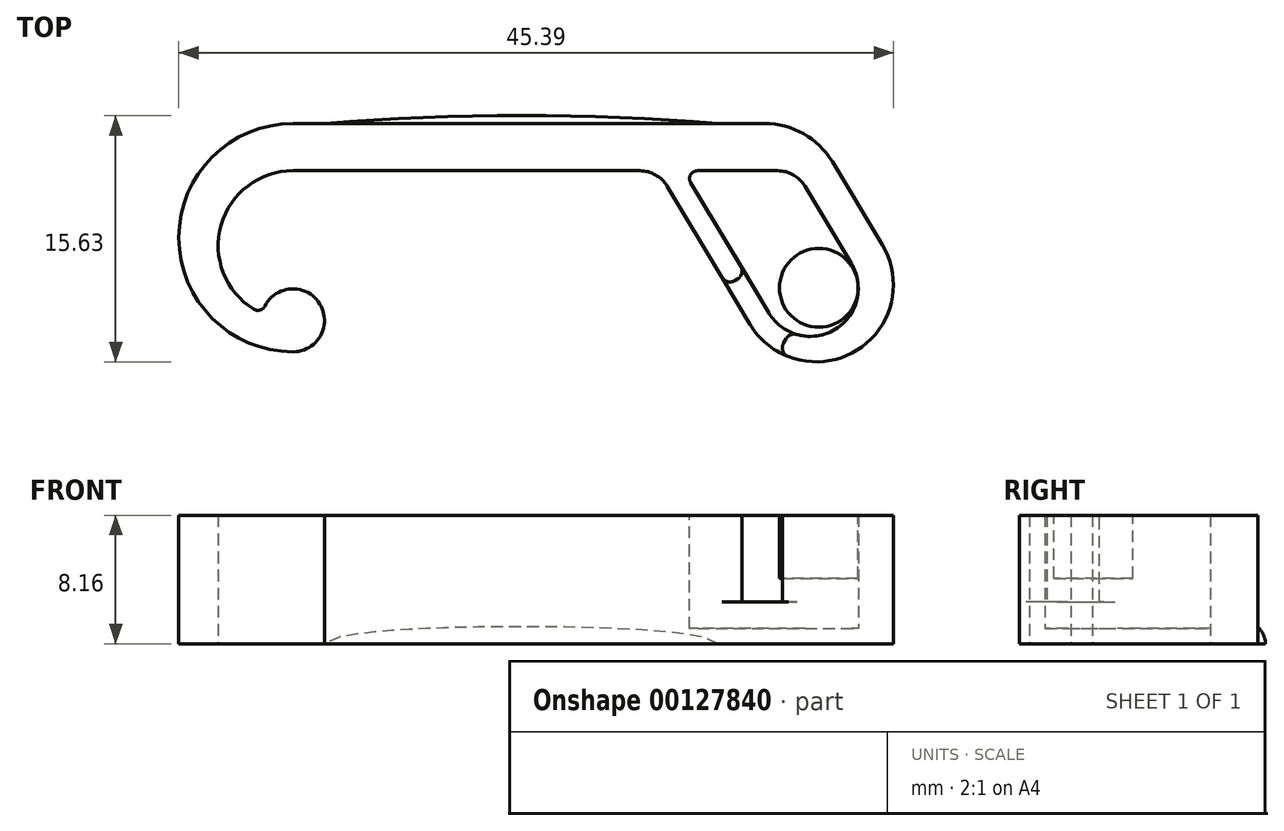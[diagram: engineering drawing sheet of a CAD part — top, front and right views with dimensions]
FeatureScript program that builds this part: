
annotation { "Feature Type Name" : "Feature", "Feature Type Description" : "" }
export const myFeature = defineFeature(function(context is Context, id is Id, definition is map)
    precondition{}
    {
        {
            var Q0;
            Q0=qCreatedBy(makeId("Top.planeOp"),FACE);
            var sketch = newSketch(context, id + "F0", { "sketchPlane" : qUnion([Q0])});
            skLineSegment(sketch, "E0", {"start": v(-39.98, 9.47) * mm, "end": v(-7.18, 9.47) * mm});
            skLineSegment(sketch, "E1", {"start": v(-7.18, 9.47) * mm, "end": v(-2.54, 1.75) * mm});
            skArc(sketch, "E2", {"start": v(-39.98, 9.47) * mm, "mid": v(-47.23, 2.22) * mm, "end": v(-39.98, -5.03) * mm});
            skArc(sketch, "E3", {"start": v(-2.54, 1.75) * mm, "mid": v(-4.22, -4.97) * mm, "end": v(-10.94, -3.3) * mm});
            skLineSegment(sketch, "E4", {"start": v(-2.54, 1.75) * mm, "end": v(-11.71, -3.76) * mm, "construction": true});
            skLineSegment(sketch, "E5", {"start": v(-10.94, -3.3) * mm, "end": v(-16.8, 6.47) * mm});
            skLineSegment(sketch, "E6", {"start": v(-39.98, 9.47) * mm, "end": v(-39.98, -5.03) * mm, "construction": true});
            skLineSegment(sketch, "E7", {"start": v(-39.98, 6.47) * mm, "end": v(-16.8, 6.47) * mm});
            skLineSegment(sketch, "E8.0", {"start": v(-8.06, 6.47) * mm, "end": v(-4.51, 0.57) * mm});
            skLineSegment(sketch, "E9.0", {"start": v(-9.74, -2.58) * mm, "end": v(-15.17, 6.47) * mm});
            skLineSegment(sketch, "E10.trimOffspring", {"start": v(-15.17, 6.47) * mm, "end": v(-8.06, 6.47) * mm});
            skArc(sketch, "E11", {"start": v(-39.98, -5.03) * mm, "mid": v(-38.42, -1.78) * mm, "end": v(-41.93, -2.61) * mm});
            skArc(sketch, "E12", {"start": v(-39.98, 6.47) * mm, "mid": v(-44.62, 2.72) * mm, "end": v(-41.93, -2.61) * mm});
            skArc(sketch, "E13", {"start": v(-9.74, -2.58) * mm, "mid": v(-5.55, -3.62) * mm, "end": v(-4.51, 0.57) * mm});
            skLineSegment(sketch, "E14", {"start": v(-37.98, -2.84) * mm, "end": v(-37.98, -7.84) * mm, "construction": true});
            skLineSegment(sketch, "E15", {"start": v(-4.08, 2.14) * mm, "end": v(-4.08, -9.58) * mm, "construction": true});
            skSolve(sketch);
        }
        {
            var Q0;
            Q0=qSketchRegion(id+"F0",true);
            extrude(context, id + "F1", {"entities" : qUnion([Q0]), "endBound" : BoundingType.SYMMETRIC, "depth" : 16.4 * mm});
        }
        {
            var Q0;
            Q0=makeQuery(id+"F0.imprint","IMPRINT",FACE,{"disambiguationData":[TD([[makeQuery(id+"F0.imprint","IMPRINT",EDGE,{"derivedFrom":sQuery(id+"F0.wireOp",EDGE,"E8.0")}),-1.0]])]});
            extrude(context, id + "F2", {"entities" : qUnion([Q0]), "operationType" : NewBodyOperationType.ADD, "endBound" : BoundingType.SYMMETRIC, "depth" : 2 * mm});
        }
        {
            var Q0;
            Q0=makeQuery(id+"F1.opExtrude","CAP_FACE",FACE,{"disambiguationData":[OSD([sQuery(id+"F0.wireOp",EDGE,"E0"),sQuery(id+"F0.wireOp",EDGE,"E1"),sQuery(id+"F0.wireOp",EDGE,"E2"),sQuery(id+"F0.wireOp",EDGE,"E3"),sQuery(id+"F0.wireOp",EDGE,"E5"),sQuery(id+"F0.wireOp",EDGE,"E7"),sQuery(id+"F0.wireOp",EDGE,"E8.0"),sQuery(id+"F0.wireOp",EDGE,"E9.0"),sQuery(id+"F0.wireOp",EDGE,"E10.trimOffspring"),sQuery(id+"F0.wireOp",EDGE,"E11"),sQuery(id+"F0.wireOp",EDGE,"E12"),sQuery(id+"F0.wireOp",EDGE,"E13")])],"isStart":false});
            var sketch = newSketch(context, id + "F3", { "sketchPlane" : qUnion([Q0])});
            skPoint(sketch, "E16", {"position": v(-6.74, -0.77) * mm});
            skLineSegment(sketch, "E17", {"start": v(-6.74, -0.77) * mm, "end": v(-10.04, -6.68) * mm});
            skLineSegment(sketch, "E18", {"start": v(-8.23, 1.7) * mm, "end": v(-13.26, -1.32) * mm});
            skLineSegment(sketch, "E19", {"start": v(-8.23, 1.7) * mm, "end": v(-6.74, -0.77) * mm});
            skLineSegment(sketch, "E20", {"start": v(-13.26, -1.32) * mm, "end": v(-10.04, -6.68) * mm});
            skArc(sketch, "E21.0", {"start": v(-2.5, 1.68) * mm, "mid": v(-4.29, -5.02) * mm, "end": v(-10.98, -3.22) * mm, "construction": true});
            skLineSegment(sketch, "E22", {"start": v(-6.74, -0.77) * mm, "end": v(-13.86, 11.08) * mm, "construction": true});
            skLineSegment(sketch, "E23.0", {"start": v(-40.2, 9.47) * mm, "end": v(-8.2, 9.47) * mm, "construction": true});
            skPoint(sketch, "E24", {"position": v(-13.36, 9.47) * mm});
            skSolve(sketch);
        }
        {
            var Q0;
            Q0=qSketchRegion(id+"F3",true);
            extrude(context, id + "F4", {"entities" : qUnion([Q0]), "operationType" : NewBodyOperationType.REMOVE, "oppositeDirection" : true, "depth" : 5.5 * mm});
        }
        {
            var Q0;
            Q0=makeQuery(id+"F1.opExtrude","CAP_FACE",FACE,{"disambiguationData":[OSD([sQuery(id+"F0.wireOp",EDGE,"E0"),sQuery(id+"F0.wireOp",EDGE,"E1"),sQuery(id+"F0.wireOp",EDGE,"E2"),sQuery(id+"F0.wireOp",EDGE,"E3"),sQuery(id+"F0.wireOp",EDGE,"E5"),sQuery(id+"F0.wireOp",EDGE,"E7"),sQuery(id+"F0.wireOp",EDGE,"E8.0"),sQuery(id+"F0.wireOp",EDGE,"E9.0"),sQuery(id+"F0.wireOp",EDGE,"E10.trimOffspring"),sQuery(id+"F0.wireOp",EDGE,"E11"),sQuery(id+"F0.wireOp",EDGE,"E12"),sQuery(id+"F0.wireOp",EDGE,"E13")])],"isStart":true});
            var sketch = newSketch(context, id + "F15", { "sketchPlane" : qUnion([Q0])});
            skLineSegment(sketch, "E25.0", {"start": v(-8.7, -1.42) * mm, "end": v(-13.39, 1.4) * mm});
            skLineSegment(sketch, "E26.0", {"start": v(-13.32, 1.21) * mm, "end": v(-10.9, 5.24) * mm});
            skLineSegment(sketch, "E27.0", {"start": v(-7.02, 1.28) * mm, "end": v(-9.79, 6.22) * mm});
            skLineSegment(sketch, "E28.0", {"start": v(-8.24, -1.73) * mm, "end": v(-6.58, 1.04) * mm});
            skSolve(sketch);
        }
        {
            var Q0;
            {var subQ0=makeQuery(id+"F1.opExtrude","CAP_EDGE",EDGE,{"disambiguationData":[OSD([sQuery(id+"F0.wireOp",EDGE,"E5")])],"isStart":true});var subQ5=sQuery(id+"F15.wireOp",EDGE,"E25.0");var subQ6=makeQuery(id+"F15.imprint","INTERSECT",VERTEX,{"derivedFrom":[subQ0,subQ5]});Q0=makeQuery(id+"F15.imprint","IMPRINT",FACE,{"disambiguationData":[TD([[makeQuery(id+"F15.imprint","IMPRINT",EDGE,{"disambiguationData":[TD([[subQ6,1.0]])],"derivedFrom":subQ5}),-1.0]])]});}
            extrude(context, id + "F16", {"entities" : qUnion([Q0]), "operationType" : NewBodyOperationType.REMOVE, "oppositeDirection" : true, "depth" : 5.5 * mm});
        }
        {
            var Q0;
            Q0=makeQuery(id+"F1.opExtrude","SWEPT_EDGE",EDGE,{"disambiguationData":[OSD([sQuery(id+"F0.wireOp",EDGE,"E5"),sQuery(id+"F0.wireOp",EDGE,"E7")])]});
            fillet(context, id + "F5", {"entities" : qUnion([Q0]), "radius" : 2 * mm, "tangentPropagation" : true, "allowEdgeOverflow" : false});
        }
        {
            var Q0;
            {var subQ0=sQuery(id+"F0.wireOp",EDGE,"E13");var subQ1=sQuery(id+"F0.wireOp",EDGE,"E10.trimOffspring");var subQ2=sQuery(id+"F0.wireOp",EDGE,"E9.0");var subQ3=sQuery(id+"F0.wireOp",EDGE,"E8.0");Q0=makeQuery(id+"F2.boolean.opBoolean","SPLIT",EDGE,{"disambiguationData":[TD([makeQuery(id+"F2.opExtrude","CAP_FACE",FACE,{"disambiguationData":[OSD([subQ3,subQ2,subQ1,subQ0])],"isStart":true})])],"derivedFrom":makeQuery(id+"F1.opExtrude","SWEPT_EDGE",EDGE,{"disambiguationData":[OSD([subQ2,subQ1])]})});}
            var Q1;
            {var subQ0=sQuery(id+"F0.wireOp",EDGE,"E13");var subQ1=sQuery(id+"F0.wireOp",EDGE,"E10.trimOffspring");var subQ2=sQuery(id+"F0.wireOp",EDGE,"E9.0");var subQ3=sQuery(id+"F0.wireOp",EDGE,"E8.0");Q1=makeQuery(id+"F2.boolean.opBoolean","SPLIT",EDGE,{"disambiguationData":[TD([makeQuery(id+"F2.opExtrude","CAP_FACE",FACE,{"disambiguationData":[OSD([subQ3,subQ2,subQ1,subQ0])],"isStart":false})])],"derivedFrom":makeQuery(id+"F1.opExtrude","SWEPT_EDGE",EDGE,{"disambiguationData":[OSD([subQ2,subQ1])]})});}
            fillet(context, id + "F17", {"entities" : qUnion([Q0, Q1]), "radius" : 0.5 * mm, "tangentPropagation" : true, "allowEdgeOverflow" : false});
        }
        {
            var Q0;
            {var subQ0=sQuery(id+"F0.wireOp",EDGE,"E13");var subQ1=sQuery(id+"F0.wireOp",EDGE,"E10.trimOffspring");var subQ2=sQuery(id+"F0.wireOp",EDGE,"E9.0");var subQ3=sQuery(id+"F0.wireOp",EDGE,"E8.0");Q0=makeQuery(id+"F2.boolean.opBoolean","SPLIT",EDGE,{"disambiguationData":[TD([makeQuery(id+"F2.opExtrude","CAP_FACE",FACE,{"disambiguationData":[OSD([subQ3,subQ2,subQ1,subQ0])],"isStart":true})])],"derivedFrom":makeQuery(id+"F1.opExtrude","SWEPT_EDGE",EDGE,{"disambiguationData":[OSD([subQ3,subQ1])]})});}
            var Q1;
            {var subQ0=sQuery(id+"F0.wireOp",EDGE,"E13");var subQ1=sQuery(id+"F0.wireOp",EDGE,"E10.trimOffspring");var subQ2=sQuery(id+"F0.wireOp",EDGE,"E9.0");var subQ3=sQuery(id+"F0.wireOp",EDGE,"E8.0");Q1=makeQuery(id+"F2.boolean.opBoolean","SPLIT",EDGE,{"disambiguationData":[TD([makeQuery(id+"F2.opExtrude","CAP_FACE",FACE,{"disambiguationData":[OSD([subQ3,subQ2,subQ1,subQ0])],"isStart":false})])],"derivedFrom":makeQuery(id+"F1.opExtrude","SWEPT_EDGE",EDGE,{"disambiguationData":[OSD([subQ3,subQ1])]})});}
            fillet(context, id + "F18", {"entities" : qUnion([Q0, Q1]), "radius" : 2 * mm, "tangentPropagation" : true, "allowEdgeOverflow" : false});
        }
        {
            var Q0;
            Q0=makeQuery(id+"F1.opExtrude","SWEPT_EDGE",EDGE,{"disambiguationData":[OSD([sQuery(id+"F0.wireOp",EDGE,"E0"),sQuery(id+"F0.wireOp",EDGE,"E1")])]});
            fillet(context, id + "F19", {"entities" : qUnion([Q0]), "radius" : 5 * mm, "tangentPropagation" : true, "allowEdgeOverflow" : false});
        }
        {
            var Q0;
            Q0=makeQuery(id+"F1.opExtrude","SWEPT_EDGE",EDGE,{"disambiguationData":[OSD([sQuery(id+"F0.wireOp",EDGE,"E11"),sQuery(id+"F0.wireOp",EDGE,"E12")])]});
            fillet(context, id + "F20", {"entities" : qUnion([Q0]), "radius" : 0.5 * mm, "tangentPropagation" : true, "allowEdgeOverflow" : false});
        }
        {
            var Q0;
            Q0=makeQuery(id+"F4.boolean.opBoolean","INTERSECT",EDGE,{"derivedFrom":[makeQuery(id+"F1.opExtrude","SWEPT_FACE",FACE,{"disambiguationData":[OSD([sQuery(id+"F0.wireOp",EDGE,"E5")])]}),makeQuery(id+"F4.opExtrude","SWEPT_FACE",FACE,{"disambiguationData":[OSD([sQuery(id+"F3.wireOp",EDGE,"E18")])]})]});
            var Q1;
            {var subQ0=sQuery(id+"F0.wireOp",EDGE,"E13");var subQ1=sQuery(id+"F0.wireOp",EDGE,"E10.trimOffspring");var subQ2=sQuery(id+"F0.wireOp",EDGE,"E9.0");var subQ3=sQuery(id+"F0.wireOp",EDGE,"E8.0");Q1=makeQuery(id+"F4.boolean.opBoolean","INTERSECT",EDGE,{"derivedFrom":[makeQuery(id+"F2.boolean.opBoolean","SPLIT",FACE,{"disambiguationData":[TD([makeQuery(id+"F2.opExtrude","CAP_FACE",FACE,{"disambiguationData":[OSD([subQ3,subQ2,subQ1,subQ0])],"isStart":false})])],"derivedFrom":makeQuery(id+"F1.opExtrude","SWEPT_FACE",FACE,{"disambiguationData":[OSD([subQ2])]})}),makeQuery(id+"F4.opExtrude","SWEPT_FACE",FACE,{"disambiguationData":[OSD([sQuery(id+"F3.wireOp",EDGE,"E18")])]})]});}
            var Q2;
            {var subQ0=sQuery(id+"F0.wireOp",EDGE,"E13");var subQ1=sQuery(id+"F0.wireOp",EDGE,"E10.trimOffspring");var subQ2=sQuery(id+"F0.wireOp",EDGE,"E9.0");var subQ3=sQuery(id+"F0.wireOp",EDGE,"E8.0");Q2=makeQuery(id+"F4.boolean.opBoolean","INTERSECT",EDGE,{"derivedFrom":[makeQuery(id+"F2.boolean.opBoolean","SPLIT",FACE,{"disambiguationData":[TD([makeQuery(id+"F2.opExtrude","CAP_FACE",FACE,{"disambiguationData":[OSD([subQ3,subQ2,subQ1,subQ0])],"isStart":false})])],"derivedFrom":makeQuery(id+"F1.opExtrude","SWEPT_FACE",FACE,{"disambiguationData":[OSD([subQ0])]})}),makeQuery(id+"F4.opExtrude","SWEPT_FACE",FACE,{"disambiguationData":[OSD([sQuery(id+"F3.wireOp",EDGE,"E17")])]})]});}
            var Q3;
            Q3=makeQuery(id+"F4.boolean.opBoolean","INTERSECT",EDGE,{"derivedFrom":[makeQuery(id+"F1.opExtrude","SWEPT_FACE",FACE,{"disambiguationData":[OSD([sQuery(id+"F0.wireOp",EDGE,"E3")])]}),makeQuery(id+"F4.opExtrude","SWEPT_FACE",FACE,{"disambiguationData":[OSD([sQuery(id+"F3.wireOp",EDGE,"E17")])]})]});
            var Q4;
            Q4=makeQuery(id+"F16.boolean.opBoolean","COPY",EDGE,{"derivedFrom":makeQuery(id+"F16.opExtrude","SWEPT_EDGE",EDGE,{"disambiguationData":[OSD([sQuery(id+"F0.wireOp",EDGE,"E3"),sQuery(id+"F15.wireOp",EDGE,"E27.0")])]})});
            var Q5;
            Q5=makeQuery(id+"F16.boolean.opBoolean","COPY",EDGE,{"derivedFrom":makeQuery(id+"F16.opExtrude","SWEPT_EDGE",EDGE,{"disambiguationData":[OSD([sQuery(id+"F0.wireOp",EDGE,"E13"),sQuery(id+"F15.wireOp",EDGE,"E27.0")])]})});
            var Q6;
            Q6=makeQuery(id+"F16.boolean.opBoolean","COPY",EDGE,{"derivedFrom":makeQuery(id+"F16.opExtrude","SWEPT_EDGE",EDGE,{"disambiguationData":[OSD([sQuery(id+"F0.wireOp",EDGE,"E5"),sQuery(id+"F15.wireOp",EDGE,"E25.0")])]})});
            var Q7;
            Q7=makeQuery(id+"F16.boolean.opBoolean","COPY",EDGE,{"derivedFrom":makeQuery(id+"F16.opExtrude","SWEPT_EDGE",EDGE,{"disambiguationData":[OSD([sQuery(id+"F0.wireOp",EDGE,"E9.0"),sQuery(id+"F15.wireOp",EDGE,"E25.0")])]})});
            fillet(context, id + "F6", {"entities" : qUnion([Q0, Q1, Q2, Q3, Q4, Q5, Q6, Q7]), "radius" : 0.6 * mm, "tangentPropagation" : true, "allowEdgeOverflow" : false});
        }
        {
            var Q0;
            Q0=qCreatedBy(makeId("Top.planeOp"),FACE);
            var sketch = newSketch(context, id + "F7", { "sketchPlane" : qUnion([Q0])});
            skLineSegment(sketch, "E29", {"start": v(-37.96, -2.7) * mm, "end": v(-37.96, 14.25) * mm, "construction": true});
            skLineSegment(sketch, "E30", {"start": v(-12.96, 3.52) * mm, "end": v(-12.96, 12.6) * mm, "construction": true});
            skLineSegment(sketch, "E31.0", {"start": v(-39.98, 9.47) * mm, "end": v(-10, 9.47) * mm});
            skPoint(sketch, "E32", {"position": v(-37.96, 9.47) * mm});
            skPoint(sketch, "E33", {"position": v(-12.96, 9.47) * mm});
            skArc(sketch, "E34", {"start": v(-12.96, 9.47) * mm, "mid": v(-25.46, 9.97) * mm, "end": v(-37.96, 9.47) * mm});
            skSolve(sketch);
        }
        {
            var Q0;
            Q0 = qSketchRegion(id + "F7", true);
            extrude(context, id + "F8", {"entities" : qUnion([Q0]), "operationType" : NewBodyOperationType.ADD, "endBound" : BoundingType.SYMMETRIC, "depth" : 3 * mm});
        }
        {
            var Q0;
            Q0=makeQuery(id+"F8.opExtrude","CAP_EDGE",EDGE,{"disambiguationData":[OSD([sQuery(id+"F7.wireOp",EDGE,"E34")])],"isStart":false});
            fillet(context, id + "F9", {"entities" : qUnion([Q0]), "radius" : 1.5 * mm, "tangentPropagation" : true, "allowEdgeOverflow" : false});
        }
        {
            var Q0;
            Q0=makeQuery(id+"F8.opExtrude","CAP_EDGE",EDGE,{"disambiguationData":[OSD([sQuery(id+"F7.wireOp",EDGE,"E34")])],"isStart":true});
            fillet(context, id + "F10", {"entities" : qUnion([Q0]), "radius" : 1.5 * mm, "tangentPropagation" : true, "allowEdgeOverflow" : false});
        }
        {
            var Q0;
            Q0=makeQuery(id+"F1.opExtrude","CAP_FACE",FACE,{"disambiguationData":[OSD([sQuery(id+"F0.wireOp",EDGE,"E0"),sQuery(id+"F0.wireOp",EDGE,"E1"),sQuery(id+"F0.wireOp",EDGE,"E2"),sQuery(id+"F0.wireOp",EDGE,"E3"),sQuery(id+"F0.wireOp",EDGE,"E5"),sQuery(id+"F0.wireOp",EDGE,"E7"),sQuery(id+"F0.wireOp",EDGE,"E8.0"),sQuery(id+"F0.wireOp",EDGE,"E9.0"),sQuery(id+"F0.wireOp",EDGE,"E10.trimOffspring"),sQuery(id+"F0.wireOp",EDGE,"E11"),sQuery(id+"F0.wireOp",EDGE,"E12"),sQuery(id+"F0.wireOp",EDGE,"E13")])],"isStart":false});
            var sketch = newSketch(context, id + "F11", { "sketchPlane" : qUnion([Q0])});
            skCircle(sketch, "E35", {"center": v(-6.58, -0.97) * mm, "radius": 2.5 * mm});
            skArc(sketch, "E36.0", {"start": v(-39.98, -5.03) * mm, "mid": v(-38.27, -1.99) * mm, "end": v(-41.76, -2.13) * mm, "construction": true});
            skArc(sketch, "E37.0", {"start": v(-7.97, -3.93) * mm, "mid": v(-4.7, -2.86) * mm, "end": v(-4.51, 0.57) * mm, "construction": true});
            skLineSegment(sketch, "E38.0", {"start": v(-39.98, 9.47) * mm, "end": v(-10, 9.47) * mm, "construction": true});
            skLineSegment(sketch, "E39", {"start": v(-39.98, -3.03) * mm, "end": v(-1.08, -0.63) * mm, "construction": true});
            skSolve(sketch);
        }
        {
            var Q0;
            Q0 = qSketchRegion(id + "F11", true);
            extrude(context, id + "F12", {"entities" : qUnion([Q0]), "oppositeDirection" : true, "depth" : 4 * mm});
        }
        {
            var Q0;
            Q0=qCreatedBy(makeId("Front.planeOp"),FACE);
            var sketch = newSketch(context, id + "F13", { "sketchPlane" : qUnion([Q0])});
            skLineSegment(sketch, "E40.bottom", {"start": v(-48.32, 0.04) * mm, "end": v(-1.2, 0.04) * mm});
            skLineSegment(sketch, "E40.top", {"start": v(-48.32, -11.32) * mm, "end": v(-1.2, -11.32) * mm});
            skLineSegment(sketch, "E40.left", {"start": v(-48.32, 0.04) * mm, "end": v(-48.32, -11.32) * mm});
            skLineSegment(sketch, "E40.right", {"start": v(-1.2, 0.04) * mm, "end": v(-1.2, -11.32) * mm});
            skSolve(sketch);
        }
        {
            var Q0;
            Q0=makeQuery(id+"F13.imprint","IMPRINT",FACE,{"disambiguationData":[TD([[makeQuery(id+"F13.imprint","IMPRINT",EDGE,{"derivedFrom":sQuery(id+"F13.wireOp",EDGE,"E40.bottom")}),-1.0]])]});
            extrude(context, id + "F14", {"entities" : qUnion([Q0]), "operationType" : NewBodyOperationType.REMOVE, "endBound" : BoundingType.THROUGH_ALL, "oppositeDirection" : true, "depth" : 25 * mm, "hasSecondDirection" : true, "secondDirectionBound" : SecondDirectionBoundingType.THROUGH_ALL, "secondDirectionOppositeDirection" : false, "secondDirectionDepth" : 25 * mm});
        }
    });
